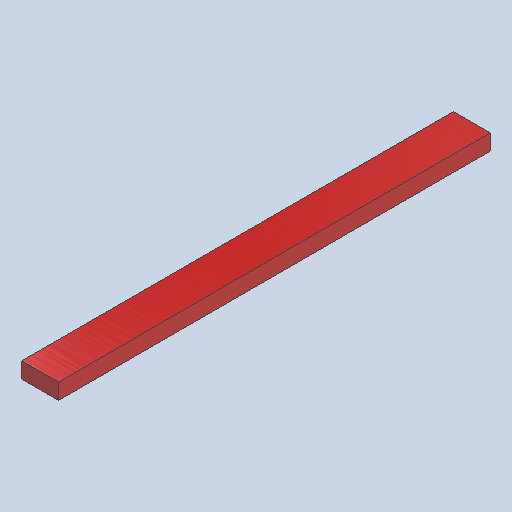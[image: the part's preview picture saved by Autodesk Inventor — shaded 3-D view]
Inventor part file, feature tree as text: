
AUTODESK INVENTOR PART (.ipt)
format: ipt  version: 2025 (Build 290162000, 162)  size: 98,304 bytes
history: native  units: in
note: dims shown in document units (in); Inventor stores cm internally (conversion verified against a paired STEP export)
features: other x4, sketch x1, plane x1
ambient origin geometry x8: Origin, YZ Plane, XZ Plane, XY Plane, X Axis, Y Axis, Z Axis, Center Point
bodies: Solid1 (feature_tree)
feature tree (6):
  other  "3'5x2x4.ipt"
  other  "Solid1::3'5x2x4.ipt"
  other  "TaggingFeature1"
  sketch  "Sketch1"  dims[d0=0.3937in]
  plane  "Work Plane1"
  other  "Finish1"
